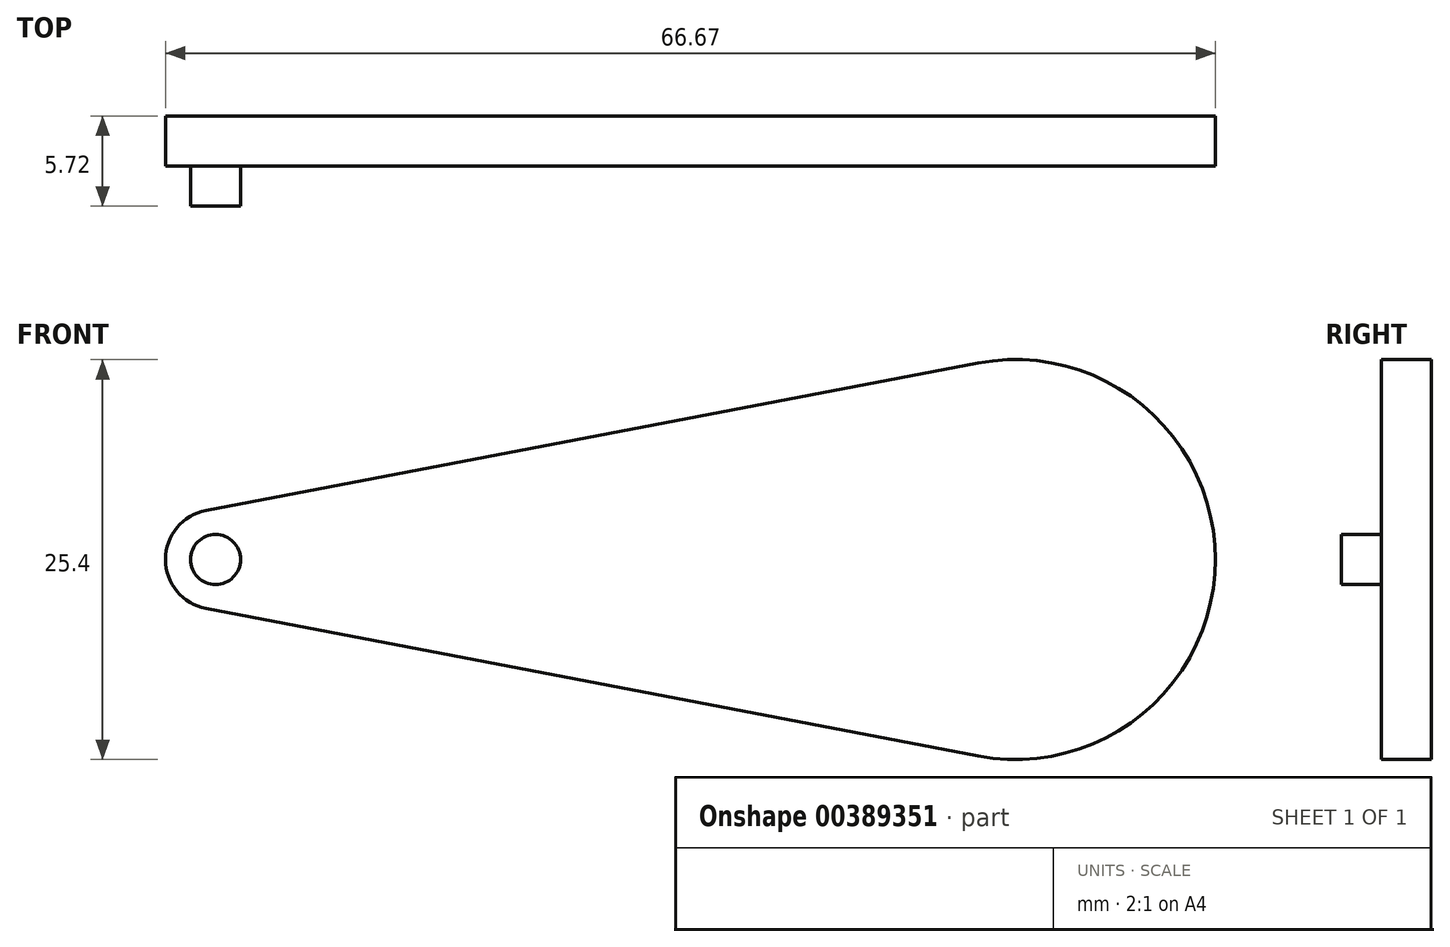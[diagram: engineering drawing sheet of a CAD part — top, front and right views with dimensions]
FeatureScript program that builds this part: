
annotation { "Feature Type Name" : "Feature", "Feature Type Description" : "" }
export const myFeature = defineFeature(function(context is Context, id is Id, definition is map)
    precondition{}
    {
        {
            var Q0;
            Q0=qCreatedBy(makeId("Front.planeOp"),FACE);
            var sketch = newSketch(context, id + "F0", { "sketchPlane" : qUnion([Q0])});
            skCircle(sketch, "E0", {"center": v(0, 0) * mm, "radius": 3.18 * mm});
            skCircle(sketch, "E1", {"center": v(50.8, 0) * mm, "radius": 12.7 * mm});
            skLineSegment(sketch, "E2", {"start": v(-0.6, 3.12) * mm, "end": v(48.42, 12.47) * mm});
            skLineSegment(sketch, "E3", {"start": v(-0.6, -3.12) * mm, "end": v(48.42, -12.47) * mm});
            skSolve(sketch);
        }
        {
            var Q0;
            Q0 = qSketchRegion(id + "F0", true);
            extrude(context, id + "F1", {"entities" : qUnion([Q0]), "depth" : 3.17 * mm});
        }
        {
            var Q0;
            Q0=makeQuery(id+"F1.opExtrude","CAP_FACE",FACE,{"disambiguationData":[OSD([sQuery(id+"F0.wireOp",EDGE,"E0"),sQuery(id+"F0.wireOp",EDGE,"E1"),sQuery(id+"F0.wireOp",EDGE,"E2"),sQuery(id+"F0.wireOp",EDGE,"E3")])],"isStart":false});
            var sketch = newSketch(context, id + "F2", { "sketchPlane" : qUnion([Q0])});
            skCircle(sketch, "E4", {"center": v(0, 0) * mm, "radius": 1.59 * mm});
            skSolve(sketch);
        }
        {
            var Q0;
            Q0 = qSketchRegion(id + "F2", true);
            extrude(context, id + "F3", {"entities" : qUnion([Q0]), "operationType" : NewBodyOperationType.ADD, "depth" : 2.54 * mm});
        }
    });
